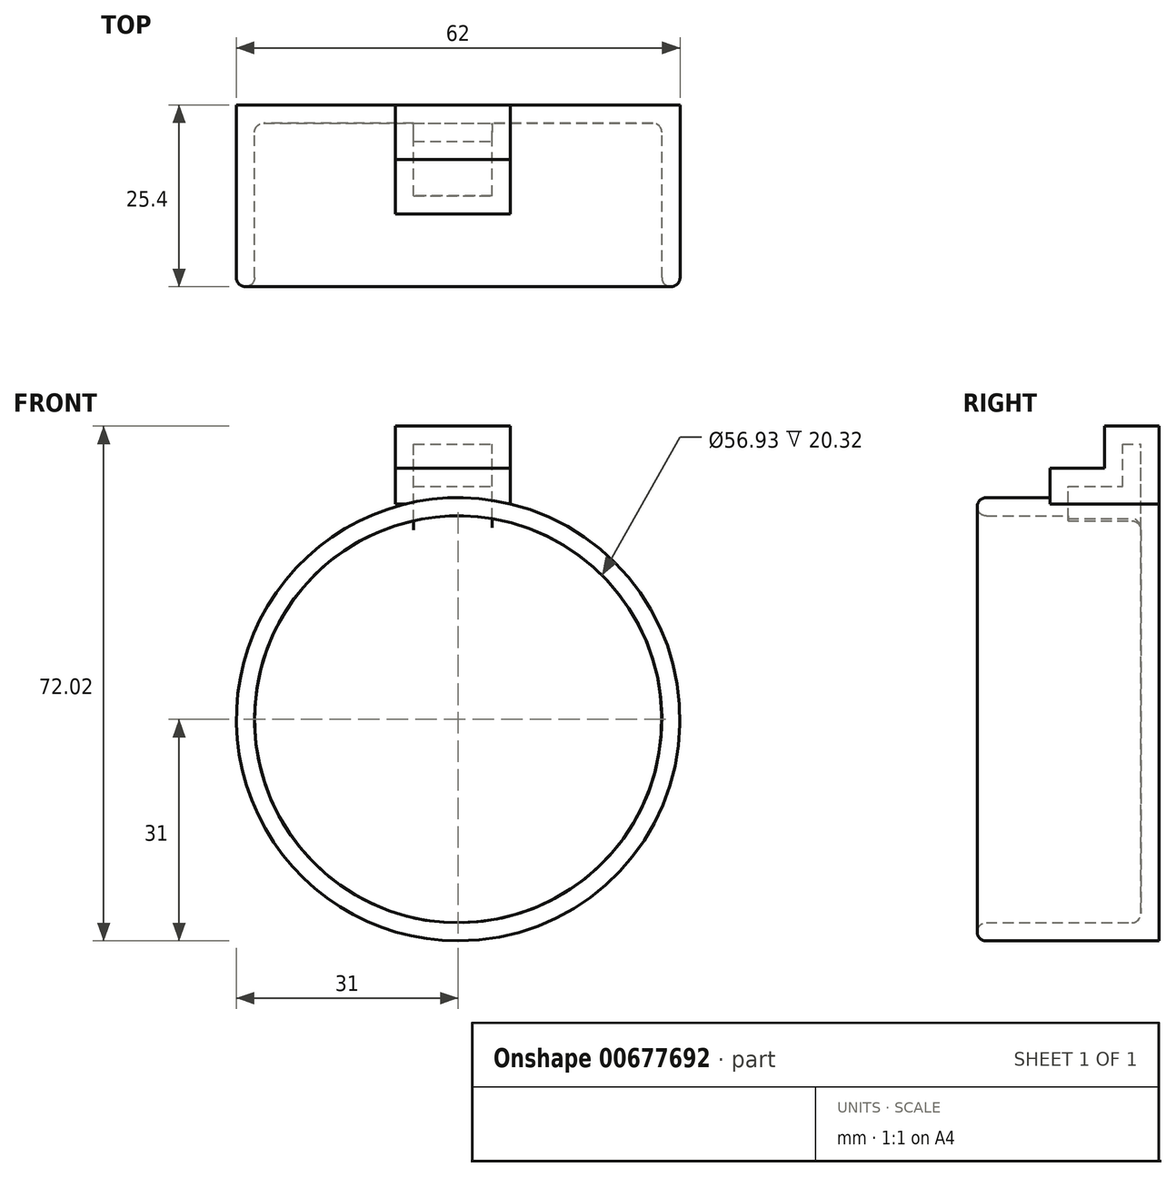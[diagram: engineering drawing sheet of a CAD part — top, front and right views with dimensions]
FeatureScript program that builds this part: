
annotation { "Feature Type Name" : "Feature", "Feature Type Description" : "" }
export const myFeature = defineFeature(function(context is Context, id is Id, definition is map)
    precondition{}
    {
        {
            var Q0;
            Q0=qCreatedBy(makeId("Front.planeOp"),FACE);
            var sketch = newSketch(context, id + "F0", { "sketchPlane" : qUnion([Q0])});
            skCircle(sketch, "E0", {"center": v(0, 0) * mm, "radius": 31 * mm});
            skLineSegment(sketch, "E1.bottom", {"start": v(-8.76, 30.14) * mm, "end": v(7.26, 30.14) * mm});
            skLineSegment(sketch, "E1.top", {"start": v(-8.76, 35.12) * mm, "end": v(7.26, 35.12) * mm});
            skLineSegment(sketch, "E1.left", {"start": v(7.26, 30.14) * mm, "end": v(7.26, 35.12) * mm});
            skLineSegment(sketch, "E1.right", {"start": v(-8.76, 30.14) * mm, "end": v(-8.76, 35.12) * mm});
            skLineSegment(sketch, "E2.top", {"start": v(-8.76, 41.02) * mm, "end": v(7.26, 41.02) * mm});
            skLineSegment(sketch, "E2.left", {"start": v(-8.76, 35.12) * mm, "end": v(-8.76, 41.02) * mm});
            skLineSegment(sketch, "E2.right", {"start": v(7.26, 35.12) * mm, "end": v(7.26, 41.02) * mm});
            skSolve(sketch);
        }
        {
            var Q0;
            {var subQ0=sQuery(id+"F0.wireOp",EDGE,"E1.bottom");var subQ1=sQuery(id+"F0.wireOp",EDGE,"E0");var subQ3=makeQuery(id+"F0.imprint","INTERSECT",VERTEX,{"derivedFrom":[subQ1,subQ0]});Q0=makeQuery(id+"F0.imprint","IMPRINT",FACE,{"disambiguationData":[TD([[makeQuery(id+"F0.imprint","IMPRINT",EDGE,{"disambiguationData":[TD([[subQ3,-1.0]])],"derivedFrom":subQ1}),1.0]])]});}
            var Q1;
            {var subQ0=sQuery(id+"F0.wireOp",EDGE,"E1.bottom");var subQ1=sQuery(id+"F0.wireOp",EDGE,"E0");var subQ3=makeQuery(id+"F0.imprint","INTERSECT",VERTEX,{"derivedFrom":[subQ1,subQ0]});Q1=makeQuery(id+"F0.imprint","IMPRINT",FACE,{"disambiguationData":[TD([[makeQuery(id+"F0.imprint","IMPRINT",EDGE,{"disambiguationData":[TD([[subQ3,1.0]])],"derivedFrom":subQ1}),1.0]])]});}
            extrude(context, id + "F1", {"entities" : qUnion([Q0, Q1]), "depth" : 25.4 * mm, "offsetDistance" : 25.4 * mm});
        }
        {
            var Q0;
            {var subQ0=sQuery(id+"F0.wireOp",EDGE,"E1.left");Q0=makeQuery(id+"F0.imprint","IMPRINT",FACE,{"disambiguationData":[TD([[makeQuery(id+"F0.imprint","IMPRINT",EDGE,{"derivedFrom":subQ0}),1.0]])]});}
            extrude(context, id + "F2", {"entities" : qUnion([Q0]), "operationType" : NewBodyOperationType.ADD, "depth" : 15.24 * mm, "offsetDistance" : 25.4 * mm});
        }
        {
            var Q0;
            Q0=makeQuery(id+"F0.imprint","IMPRINT",FACE,{"disambiguationData":[TD([[makeQuery(id+"F0.imprint","IMPRINT",EDGE,{"derivedFrom":sQuery(id+"F0.wireOp",EDGE,"E1.top")}),1.0]])]});
            extrude(context, id + "F3", {"entities" : qUnion([Q0]), "operationType" : NewBodyOperationType.ADD, "depth" : 7.62 * mm, "offsetDistance" : 25.4 * mm});
        }
        {
            var Q0;
            Q0=makeQuery(id+"F1.opExtrude","CAP_FACE",FACE,{"disambiguationData":[OSD([sQuery(id+"F0.wireOp",EDGE,"E0")])],"isStart":false});
            shell(context, id + "F4", {"entities" : qUnion([Q0]), "thickness" : 2.54 * mm});
        }
        {
            var Q0;
            {var subQ0=sQuery(id+"F0.wireOp",EDGE,"E0");Q0=makeQuery(id+"F4.opShell","OFFSET_EDGE",EDGE,{"disambiguationData":[OSD([subQ0]),TDD([makeQuery(id+"F1.opExtrude","CAP_EDGE",EDGE,{"disambiguationData":[OSD([subQ0])],"isStart":false})])]});}
            var Q1;
            Q1=makeQuery(id+"F1.opExtrude","CAP_EDGE",EDGE,{"disambiguationData":[OSD([sQuery(id+"F0.wireOp",EDGE,"E0")])],"isStart":false});
            var Q2;
            {var subQ0=sQuery(id+"F0.wireOp",EDGE,"E0");Q2=makeQuery(id+"F4.opShell","OFFSET_EDGE",EDGE,{"disambiguationData":[OSD([subQ0]),TDD([makeQuery(id+"F1.opExtrude","CAP_EDGE",EDGE,{"disambiguationData":[OSD([subQ0])],"isStart":true})])]});}
            fillet(context, id + "F5", {"entities" : qUnion([Q0, Q1, Q2]), "radius" : 1.27 * mm, "tangentPropagation" : true, "allowEdgeOverflow" : false});
        }
    });
